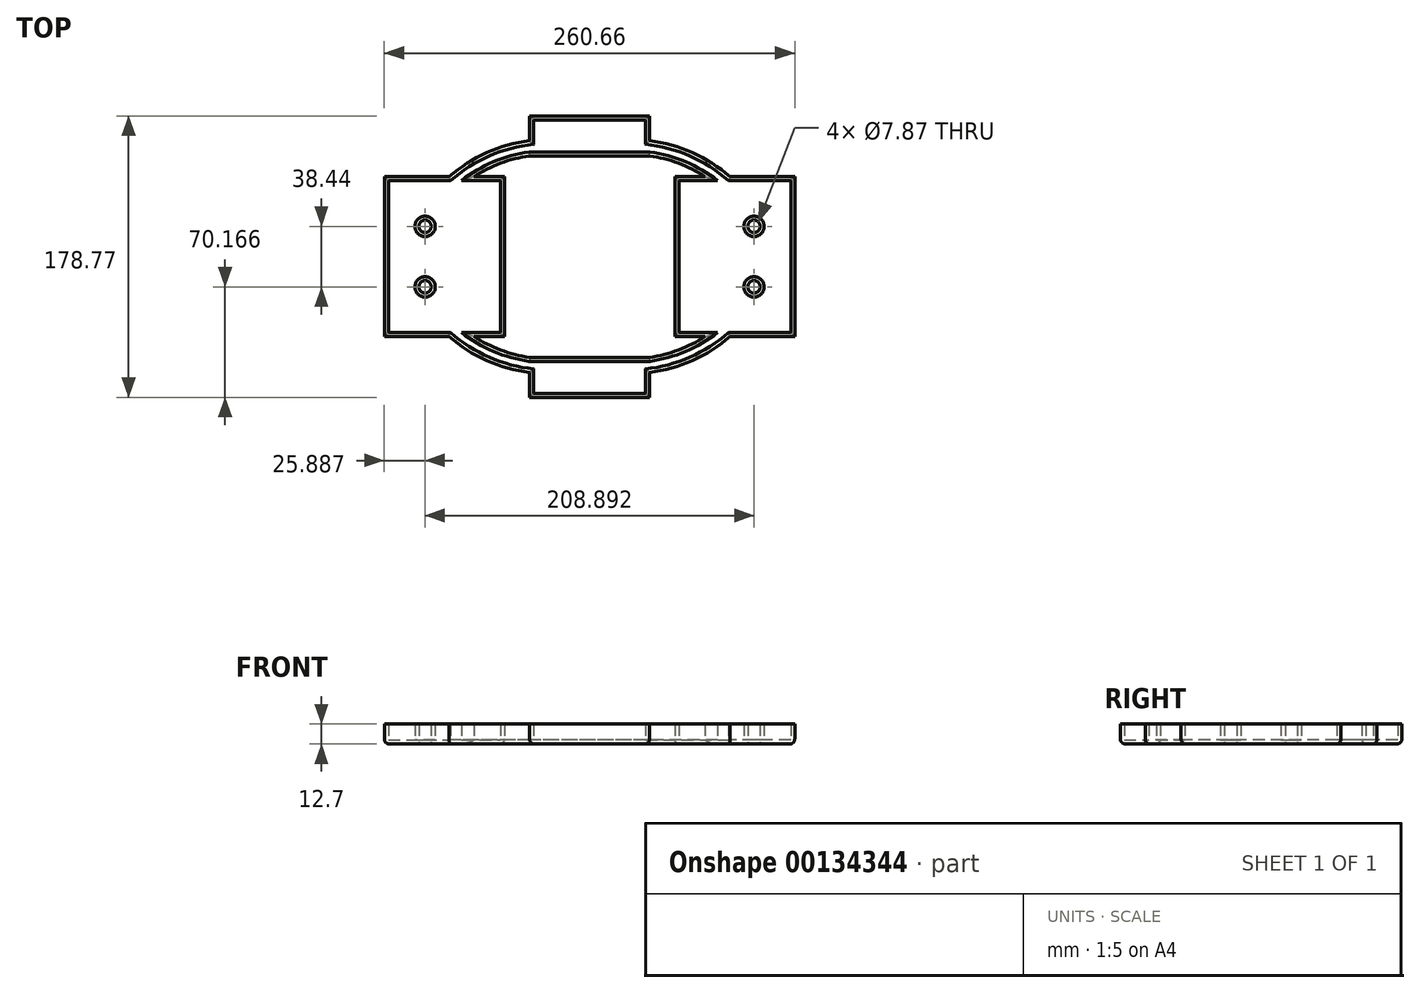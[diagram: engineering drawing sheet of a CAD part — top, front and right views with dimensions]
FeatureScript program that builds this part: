
annotation { "Feature Type Name" : "Feature", "Feature Type Description" : "" }
export const myFeature = defineFeature(function(context is Context, id is Id, definition is map)
    precondition{}
    {
        {
            var Q0;
            Q0=qCreatedBy(makeId("Top.planeOp"),FACE);
            var sketch = newSketch(context, id + "F0", { "sketchPlane" : qUnion([Q0])});
            skLineSegment(sketch, "E0.bottom", {"start": v(-29.86, -45.48) * mm, "end": v(11.24, -45.48) * mm});
            skLineSegment(sketch, "E0.top", {"start": v(-29.86, -96.28) * mm, "end": v(46.34, -96.28) * mm});
            skLineSegment(sketch, "E0.left", {"start": v(-29.86, -45.48) * mm, "end": v(-29.86, -96.28) * mm});
            skLineSegment(sketch, "E0.right", {"start": v(46.34, -45.48) * mm, "end": v(46.34, -96.28) * mm});
            skLineSegment(sketch, "E1.bottom", {"start": v(100.47, -6.9) * mm, "end": v(62.37, -6.9) * mm});
            skLineSegment(sketch, "E1.top", {"start": v(100.47, -32.3) * mm, "end": v(62.37, -32.3) * mm});
            skLineSegment(sketch, "E1.left", {"start": v(100.47, -6.9) * mm, "end": v(100.47, -32.3) * mm});
            skLineSegment(sketch, "E1.right", {"start": v(62.37, -6.9) * mm, "end": v(62.37, -22.69) * mm});
            skCircle(sketch, "E2", {"center": v(-3.97, -77.06) * mm, "radius": 3.94 * mm});
            skArc(sketch, "E3", {"start": v(62.37, -22.69) * mm, "mid": v(35.13, -30.32) * mm, "end": v(11.24, -45.48) * mm});
            skArc(sketch, "E4.0", {"start": v(62.37, -32.3) * mm, "mid": v(44, -36.97) * mm, "end": v(27.08, -45.48) * mm});
            skLineSegment(sketch, "E5.trimOffspring", {"start": v(27.08, -45.48) * mm, "end": v(46.34, -45.48) * mm});
            skSolve(sketch);
        }
        {
            var Q0;
            Q0=makeQuery(id+"F0.imprint","IMPRINT",FACE,{"disambiguationData":[TD([[makeQuery(id+"F0.imprint","IMPRINT",EDGE,{"derivedFrom":sQuery(id+"F0.wireOp",EDGE,"E0.bottom")}),-1.0]])]});
            extrude(context, id + "F1", {"entities" : qUnion([Q0]), "depth" : 12.7 * mm});
        }
        {
            var Q0;
            Q0=makeQuery(id+"F1.opExtrude","SWEPT_BODY",BODY,{"disambiguationData":[OSD([sQuery(id+"F0.wireOp",EDGE,"E0.bottom"),sQuery(id+"F0.wireOp",EDGE,"E0.top"),sQuery(id+"F0.wireOp",EDGE,"E0.left"),sQuery(id+"F0.wireOp",EDGE,"E0.right"),sQuery(id+"F0.wireOp",EDGE,"E1.bottom"),sQuery(id+"F0.wireOp",EDGE,"E1.top"),sQuery(id+"F0.wireOp",EDGE,"E1.left"),sQuery(id+"F0.wireOp",EDGE,"E1.right"),sQuery(id+"F0.wireOp",EDGE,"E2"),sQuery(id+"F0.wireOp",EDGE,"E3"),sQuery(id+"F0.wireOp",EDGE,"E4.0"),sQuery(id+"F0.wireOp",EDGE,"E5.trimOffspring")])]});
            var Q1;
            Q1=makeQuery(id+"F1.opExtrude","SWEPT_FACE",FACE,{"disambiguationData":[OSD([sQuery(id+"F0.wireOp",EDGE,"E0.top")])]});
            mirror(context, id + "F2", {"operationType" : NewBodyOperationType.ADD, "entities" : qUnion([Q0]), "mirrorPlane" : qUnion([Q1])});
        }
        {
            var Q0;
            Q0=makeQuery(id+"F1.opExtrude","SWEPT_BODY",BODY,{"disambiguationData":[OSD([sQuery(id+"F0.wireOp",EDGE,"E0.bottom"),sQuery(id+"F0.wireOp",EDGE,"E0.top"),sQuery(id+"F0.wireOp",EDGE,"E0.left"),sQuery(id+"F0.wireOp",EDGE,"E0.right"),sQuery(id+"F0.wireOp",EDGE,"E1.bottom"),sQuery(id+"F0.wireOp",EDGE,"E1.top"),sQuery(id+"F0.wireOp",EDGE,"E1.left"),sQuery(id+"F0.wireOp",EDGE,"E1.right"),sQuery(id+"F0.wireOp",EDGE,"E2"),sQuery(id+"F0.wireOp",EDGE,"E3"),sQuery(id+"F0.wireOp",EDGE,"E4.0"),sQuery(id+"F0.wireOp",EDGE,"E5.trimOffspring")])]});
            var Q1;
            Q1=makeQuery(id+"F2.opPattern","COPY",FACE,{"derivedFrom":makeQuery(id+"F1.opExtrude","SWEPT_FACE",FACE,{"disambiguationData":[OSD([sQuery(id+"F0.wireOp",EDGE,"E1.left")])]}),"instanceName":"1"});
            mirror(context, id + "F3", {"operationType" : NewBodyOperationType.ADD, "entities" : qUnion([Q0]), "mirrorPlane" : qUnion([Q1])});
        }
        {
            var Q0;
            {var subQ0=makeQuery(id+"F1.opExtrude","CAP_FACE",FACE,{"disambiguationData":[OSD([sQuery(id+"F0.wireOp",EDGE,"E0.bottom"),sQuery(id+"F0.wireOp",EDGE,"E0.top"),sQuery(id+"F0.wireOp",EDGE,"E0.left"),sQuery(id+"F0.wireOp",EDGE,"E0.right"),sQuery(id+"F0.wireOp",EDGE,"E1.bottom"),sQuery(id+"F0.wireOp",EDGE,"E1.top"),sQuery(id+"F0.wireOp",EDGE,"E1.left"),sQuery(id+"F0.wireOp",EDGE,"E1.right"),sQuery(id+"F0.wireOp",EDGE,"E2"),sQuery(id+"F0.wireOp",EDGE,"E3"),sQuery(id+"F0.wireOp",EDGE,"E4.0"),sQuery(id+"F0.wireOp",EDGE,"E5.trimOffspring")])],"isStart":false});var subQ1=makeQuery(id+"F2.boolean.opBoolean","MERGE",FACE,{"derivedFrom":[subQ0,makeQuery(id+"F2.opPattern","COPY",FACE,{"derivedFrom":subQ0,"instanceName":"1"})]});Q0=makeQuery(id+"F3.boolean.opBoolean","MERGE",FACE,{"derivedFrom":[subQ1,makeQuery(id+"F3.opPattern","COPY",FACE,{"derivedFrom":subQ1,"instanceName":"1"})]});}
            shell(context, id + "F4", {"entities" : qUnion([Q0]), "thickness" : 2.54 * mm});
        }
        {
            var Q0;
            {var subQ0=makeQuery(id+"F1.opExtrude","CAP_EDGE",EDGE,{"disambiguationData":[OSD([sQuery(id+"F0.wireOp",EDGE,"E0.left")])],"isStart":true});Q0=makeQuery(id+"F2.boolean.opBoolean","MERGE",EDGE,{"derivedFrom":[subQ0,makeQuery(id+"F2.opPattern","COPY",EDGE,{"derivedFrom":subQ0,"instanceName":"1"})]});}
            var Q1;
            Q1=makeQuery(id+"F1.opExtrude","CAP_EDGE",EDGE,{"disambiguationData":[OSD([sQuery(id+"F0.wireOp",EDGE,"E0.bottom")])],"isStart":true});
            var Q2;
            Q2=makeQuery(id+"F1.opExtrude","CAP_EDGE",EDGE,{"disambiguationData":[OSD([sQuery(id+"F0.wireOp",EDGE,"E3")])],"isStart":true});
            var Q3;
            Q3=makeQuery(id+"F1.opExtrude","CAP_EDGE",EDGE,{"disambiguationData":[OSD([sQuery(id+"F0.wireOp",EDGE,"E1.right")])],"isStart":true});
            var Q4;
            {var subQ0=makeQuery(id+"F1.opExtrude","CAP_EDGE",EDGE,{"disambiguationData":[OSD([sQuery(id+"F0.wireOp",EDGE,"E1.bottom")])],"isStart":true});Q4=makeQuery(id+"F3.boolean.opBoolean","MERGE",EDGE,{"derivedFrom":[subQ0,makeQuery(id+"F3.opPattern","COPY",EDGE,{"derivedFrom":subQ0,"instanceName":"1"})]});}
            var Q5;
            Q5=makeQuery(id+"F3.opPattern","COPY",EDGE,{"derivedFrom":makeQuery(id+"F1.opExtrude","CAP_EDGE",EDGE,{"disambiguationData":[OSD([sQuery(id+"F0.wireOp",EDGE,"E1.right")])],"isStart":true}),"instanceName":"1"});
            var Q6;
            Q6=makeQuery(id+"F3.opPattern","COPY",EDGE,{"derivedFrom":makeQuery(id+"F1.opExtrude","CAP_EDGE",EDGE,{"disambiguationData":[OSD([sQuery(id+"F0.wireOp",EDGE,"E3")])],"isStart":true}),"instanceName":"1"});
            var Q7;
            Q7=makeQuery(id+"F3.opPattern","COPY",EDGE,{"derivedFrom":makeQuery(id+"F1.opExtrude","CAP_EDGE",EDGE,{"disambiguationData":[OSD([sQuery(id+"F0.wireOp",EDGE,"E0.bottom")])],"isStart":true}),"instanceName":"1"});
            var Q8;
            {var subQ0=makeQuery(id+"F1.opExtrude","CAP_EDGE",EDGE,{"disambiguationData":[OSD([sQuery(id+"F0.wireOp",EDGE,"E0.left")])],"isStart":true});Q8=makeQuery(id+"F3.opPattern","COPY",EDGE,{"derivedFrom":makeQuery(id+"F2.boolean.opBoolean","MERGE",EDGE,{"derivedFrom":[subQ0,makeQuery(id+"F2.opPattern","COPY",EDGE,{"derivedFrom":subQ0,"instanceName":"1"})]}),"instanceName":"1"});}
            var Q9;
            Q9=makeQuery(id+"F3.opPattern","COPY",EDGE,{"derivedFrom":makeQuery(id+"F2.opPattern","COPY",EDGE,{"derivedFrom":makeQuery(id+"F1.opExtrude","CAP_EDGE",EDGE,{"disambiguationData":[OSD([sQuery(id+"F0.wireOp",EDGE,"E0.bottom")])],"isStart":true}),"instanceName":"1"}),"instanceName":"1"});
            var Q10;
            Q10=makeQuery(id+"F3.opPattern","COPY",EDGE,{"derivedFrom":makeQuery(id+"F2.opPattern","COPY",EDGE,{"derivedFrom":makeQuery(id+"F1.opExtrude","CAP_EDGE",EDGE,{"disambiguationData":[OSD([sQuery(id+"F0.wireOp",EDGE,"E3")])],"isStart":true}),"instanceName":"1"}),"instanceName":"1"});
            var Q11;
            Q11=makeQuery(id+"F3.opPattern","COPY",EDGE,{"derivedFrom":makeQuery(id+"F2.opPattern","COPY",EDGE,{"derivedFrom":makeQuery(id+"F1.opExtrude","CAP_EDGE",EDGE,{"disambiguationData":[OSD([sQuery(id+"F0.wireOp",EDGE,"E1.right")])],"isStart":true}),"instanceName":"1"}),"instanceName":"1"});
            var Q12;
            {var subQ0=makeQuery(id+"F2.opPattern","COPY",EDGE,{"derivedFrom":makeQuery(id+"F1.opExtrude","CAP_EDGE",EDGE,{"disambiguationData":[OSD([sQuery(id+"F0.wireOp",EDGE,"E1.bottom")])],"isStart":true}),"instanceName":"1"});Q12=makeQuery(id+"F3.boolean.opBoolean","MERGE",EDGE,{"derivedFrom":[subQ0,makeQuery(id+"F3.opPattern","COPY",EDGE,{"derivedFrom":subQ0,"instanceName":"1"})]});}
            var Q13;
            Q13=makeQuery(id+"F2.opPattern","COPY",EDGE,{"derivedFrom":makeQuery(id+"F1.opExtrude","CAP_EDGE",EDGE,{"disambiguationData":[OSD([sQuery(id+"F0.wireOp",EDGE,"E1.right")])],"isStart":true}),"instanceName":"1"});
            var Q14;
            Q14=makeQuery(id+"F2.opPattern","COPY",EDGE,{"derivedFrom":makeQuery(id+"F1.opExtrude","CAP_EDGE",EDGE,{"disambiguationData":[OSD([sQuery(id+"F0.wireOp",EDGE,"E3")])],"isStart":true}),"instanceName":"1"});
            var Q15;
            Q15=makeQuery(id+"F2.opPattern","COPY",EDGE,{"derivedFrom":makeQuery(id+"F1.opExtrude","CAP_EDGE",EDGE,{"disambiguationData":[OSD([sQuery(id+"F0.wireOp",EDGE,"E0.bottom")])],"isStart":true}),"instanceName":"1"});
            var Q16;
            Q16=makeQuery(id+"F2.opPattern","COPY",EDGE,{"derivedFrom":makeQuery(id+"F1.opExtrude","CAP_EDGE",EDGE,{"disambiguationData":[OSD([sQuery(id+"F0.wireOp",EDGE,"E4.0")])],"isStart":true}),"instanceName":"1"});
            var Q17;
            Q17=makeQuery(id+"F2.opPattern","COPY",EDGE,{"derivedFrom":makeQuery(id+"F1.opExtrude","CAP_EDGE",EDGE,{"disambiguationData":[OSD([sQuery(id+"F0.wireOp",EDGE,"E5.trimOffspring")])],"isStart":true}),"instanceName":"1"});
            var Q18;
            {var subQ0=makeQuery(id+"F1.opExtrude","CAP_EDGE",EDGE,{"disambiguationData":[OSD([sQuery(id+"F0.wireOp",EDGE,"E0.right")])],"isStart":true});Q18=makeQuery(id+"F2.boolean.opBoolean","MERGE",EDGE,{"derivedFrom":[subQ0,makeQuery(id+"F2.opPattern","COPY",EDGE,{"derivedFrom":subQ0,"instanceName":"1"})]});}
            var Q19;
            Q19=makeQuery(id+"F1.opExtrude","CAP_EDGE",EDGE,{"disambiguationData":[OSD([sQuery(id+"F0.wireOp",EDGE,"E5.trimOffspring")])],"isStart":true});
            var Q20;
            Q20=makeQuery(id+"F1.opExtrude","CAP_EDGE",EDGE,{"disambiguationData":[OSD([sQuery(id+"F0.wireOp",EDGE,"E4.0")])],"isStart":true});
            var Q21;
            {var subQ0=makeQuery(id+"F1.opExtrude","CAP_EDGE",EDGE,{"disambiguationData":[OSD([sQuery(id+"F0.wireOp",EDGE,"E1.top")])],"isStart":true});Q21=makeQuery(id+"F3.boolean.opBoolean","MERGE",EDGE,{"derivedFrom":[subQ0,makeQuery(id+"F3.opPattern","COPY",EDGE,{"derivedFrom":subQ0,"instanceName":"1"})]});}
            var Q22;
            Q22=makeQuery(id+"F3.opPattern","COPY",EDGE,{"derivedFrom":makeQuery(id+"F1.opExtrude","CAP_EDGE",EDGE,{"disambiguationData":[OSD([sQuery(id+"F0.wireOp",EDGE,"E4.0")])],"isStart":true}),"instanceName":"1"});
            var Q23;
            Q23=makeQuery(id+"F3.opPattern","COPY",EDGE,{"derivedFrom":makeQuery(id+"F1.opExtrude","CAP_EDGE",EDGE,{"disambiguationData":[OSD([sQuery(id+"F0.wireOp",EDGE,"E5.trimOffspring")])],"isStart":true}),"instanceName":"1"});
            var Q24;
            {var subQ0=makeQuery(id+"F1.opExtrude","CAP_EDGE",EDGE,{"disambiguationData":[OSD([sQuery(id+"F0.wireOp",EDGE,"E0.right")])],"isStart":true});Q24=makeQuery(id+"F3.opPattern","COPY",EDGE,{"derivedFrom":makeQuery(id+"F2.boolean.opBoolean","MERGE",EDGE,{"derivedFrom":[subQ0,makeQuery(id+"F2.opPattern","COPY",EDGE,{"derivedFrom":subQ0,"instanceName":"1"})]}),"instanceName":"1"});}
            var Q25;
            Q25=makeQuery(id+"F3.opPattern","COPY",EDGE,{"derivedFrom":makeQuery(id+"F2.opPattern","COPY",EDGE,{"derivedFrom":makeQuery(id+"F1.opExtrude","CAP_EDGE",EDGE,{"disambiguationData":[OSD([sQuery(id+"F0.wireOp",EDGE,"E5.trimOffspring")])],"isStart":true}),"instanceName":"1"}),"instanceName":"1"});
            var Q26;
            Q26=makeQuery(id+"F3.opPattern","COPY",EDGE,{"derivedFrom":makeQuery(id+"F2.opPattern","COPY",EDGE,{"derivedFrom":makeQuery(id+"F1.opExtrude","CAP_EDGE",EDGE,{"disambiguationData":[OSD([sQuery(id+"F0.wireOp",EDGE,"E4.0")])],"isStart":true}),"instanceName":"1"}),"instanceName":"1"});
            var Q27;
            {var subQ0=makeQuery(id+"F2.opPattern","COPY",EDGE,{"derivedFrom":makeQuery(id+"F1.opExtrude","CAP_EDGE",EDGE,{"disambiguationData":[OSD([sQuery(id+"F0.wireOp",EDGE,"E1.top")])],"isStart":true}),"instanceName":"1"});Q27=makeQuery(id+"F3.boolean.opBoolean","MERGE",EDGE,{"derivedFrom":[subQ0,makeQuery(id+"F3.opPattern","COPY",EDGE,{"derivedFrom":subQ0,"instanceName":"1"})]});}
            fillet(context, id + "F5", {"entities" : qUnion([Q0, Q1, Q2, Q3, Q4, Q5, Q6, Q7, Q8, Q9, Q10, Q11, Q12, Q13, Q14, Q15, Q16, Q17, Q18, Q19, Q20, Q21, Q22, Q23, Q24, Q25, Q26, Q27]), "radius" : 3.17 * mm, "tangentPropagation" : true, "allowEdgeOverflow" : false});
        }
    });
